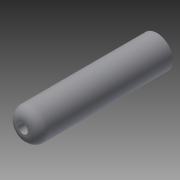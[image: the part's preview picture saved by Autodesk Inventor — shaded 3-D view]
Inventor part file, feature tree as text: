
AUTODESK INVENTOR PART (.ipt)
format: ipt  version: 2014 SP1 (Build 180222100, 222)  size: 89,600 bytes
history: native  units: in
note: dims shown in document units (in); Inventor stores cm internally (conversion verified against a paired STEP export)
features: extrude x1, fillet x1, sketch x1
ambient origin geometry x8: Origin, YZ Plane, XZ Plane, XY Plane, X Axis, Y Axis, Z Axis, Center Point
bodies: Solid1 (feature_tree)
feature tree (3):
  extrude  "Extrusion1"  Depth=0.75in
  fillet  "Fillet1"  Radius=10.5in
  sketch  "Sketch1"  dims[d0=2.5in d1=0.75in d2=10.5in d3=0.0in d4=0.75in]
